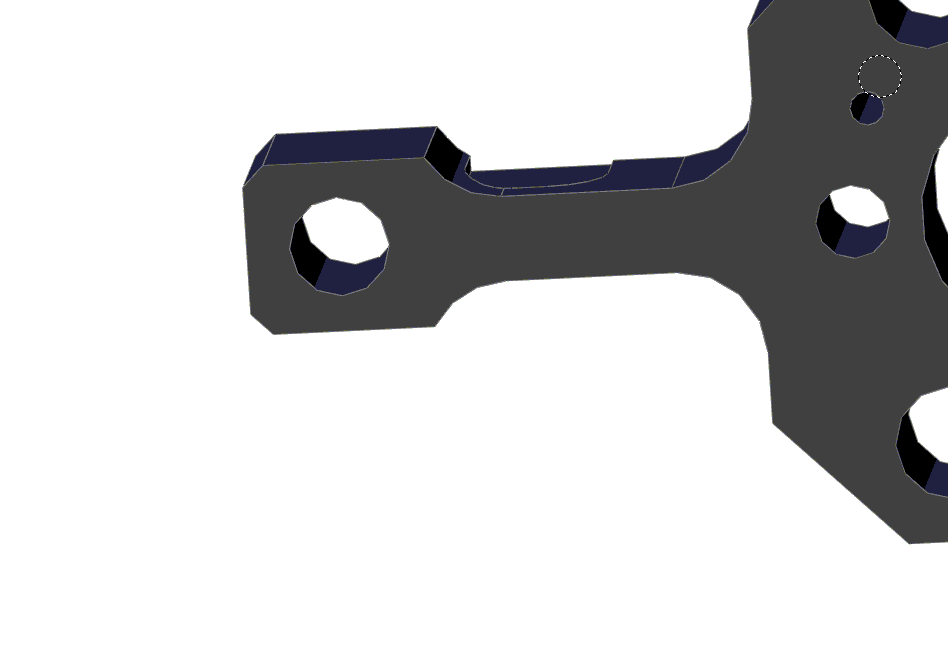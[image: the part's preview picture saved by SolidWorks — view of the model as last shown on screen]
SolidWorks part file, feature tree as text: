
SOLIDWORKS PART (.sldprt)
format: sldprt  version: not decoded by parser v0  size: 419,840 bytes
history: native  units: mm
features: sketch x11, cut_extrude x5, plane x4, chamfer x2, material x1, extrude x1, thread x1 (+9 scaffold rows collapsed)
feature tree (34):
  scaffold x9  (default folders/planes/origin — collapsed)
  material  "Matériau <non spécifié>"
  plane  "Plan1"
  plane  "Plan2"
  plane  "Plan3"
  sketch  "Esquisse1"  dims[c1.D1=56.0mm c1.D2=46.0mm c2.D1=56.0mm c2.D3=12.0mm c2.D4=17.0mm c2.D5=20.0mm]
  extrude  "Base-Extrusion"  Depth=12mm
  sketch  "Esquisse4"  dims[c1.D1=18.4mm c1.D2=18.4mm c1.D3=9.2mm c2.D2=23.0mm c2.D1=8.7mm c3.D2=23.0mm]
  cut_extrude  "Enlèv. mat.-Extru.3"  Depth=12mm
  sketch  "Esquisse6"  dims[c1.D1=~7.113348mm c1.D2=12.0mm c1.D3=12.0mm c2.D1=12.0mm c2.D3=6.0mm c2.D4=12.0mm c2.D5=~5.119496mm c3.D5=45.0deg c3.D6=11.0mm c3.D7=11.0mm c3.D8=20.0mm c3.D9=3.0mm]
  cut_extrude  "Enlèv. mat.-Extru.4"  [1 undecoded]
  chamfer  "Chanfrein6"  Distance=1.5mm Angle=45deg
  chamfer  "Chanfrein7"  Distance=1.5mm Angle=45deg
  sketch  "Esquisse7"  dims[D1=8.0mm D2=7.0mm D3=7.5mm]
  sketch  "Esquisse8"  dims[c1.D1=8.0mm c1.D2=7.0mm c1.D3=7.5mm c2.D1=12.0mm]
  sketch  "Esquisse9"  dims[c1.D1=5.2mm c1.D2=13.5mm c1.D3=23.0mm c2.D1=12.0mm]
  sketch  "Esquisse10"  dims[c1.D1=7.0mm c1.D2=42.0mm c2.D1=12.0mm]
  sketch  "Esquisse11"  dims[D1=2.4mm D2=8.0mm D3=12.0mm]
  thread  "Représentation de filetage1"  Diameter=12mm  [1 undecoded]
  sketch  "Esquisse12"  dims[D4=4.0mm D1=31.0mm D2=10.0mm D3=9.0mm]
  cut_extrude  "Enlèv. mat.-Extru.5"  Depth=0.3mm
  sketch  "Esquisse13"  dims[D1=0.0mm]
  cut_extrude  "Enlèv. mat.-Extru.6"  [1 undecoded]
  plane  "Plan4"  Offset=0.3mm
  sketch  "Esquisse14"  dims[D1=0.0mm]
  cut_extrude  "Enlèv. mat.-Extru.7"  [1 undecoded]
decode coverage: 17 of 20 modeling features carry decoded parameters
note: ~ marks probable driven/reference dimensions
note: 4 parameter values undecoded
summary: no parameter record found for 3 features
note: suppression state not decoded; provenance and decode notes live in map.json
